# Revit family: Urbane II - Hand Wall Basin Integrated Rail
name_source: partatom
category: Specialty Equipment
units: mm (PartAtom-declared; Revit-internal decimal feet)

## family parameters
Cut with Voids When Loaded = No
Host = Face
OmniClass Number = 23.40.20.21.27
OmniClass Title = Towel Bars
Part Type = Normal
Room Calculation Point = No
Round Connector Dimension = Use Radius
Shared = No

## types (5) — shared parameters
Assembly Code = C1030220
Default Elevation = 1000 mm  [stored 3.28084 ft]
Manufacturer = GWA Bathrooms & Kitchens
RailWidth = 428 mm  [stored 1.4042 ft]
URL = https://www.caroma.com.au

## per-type parameters (varying)
| type | Material_Base | Model |
| Urbane II - Hand Wall Basin Integrated Rail - Chrome | GWA_Metal-Chrome | 99623C |
| Urbane II - Hand Wall Basin Integrated Rail - Matte Black | GWA-Metal-Black | 99623B |
| Urbane II - Hand Wall Basin Integrated Rail - Brushed Brass | GWA_Metal-Brushed-Brass | 99623BR |
| Urbane II - Hand Wall Basin Integrated Rail - Gunmetal | GWA-Metal-Gunmetal Grey | 99623GM |
| Urbane II - Hand Wall Basin Integrated Rail - Brushed Nickel | GWA_Metal-Brushed-Nickel | 99623BN |

note: column(s) folded — value = type name in every type: Description

note: [stored X ft] marks values corroborated as IEEE doubles in the binary element streams (Revit-internal decimal feet)

## geometry (parser evidence)
native form markers: Sweep x2
no freeform markers — native parametric forms only
